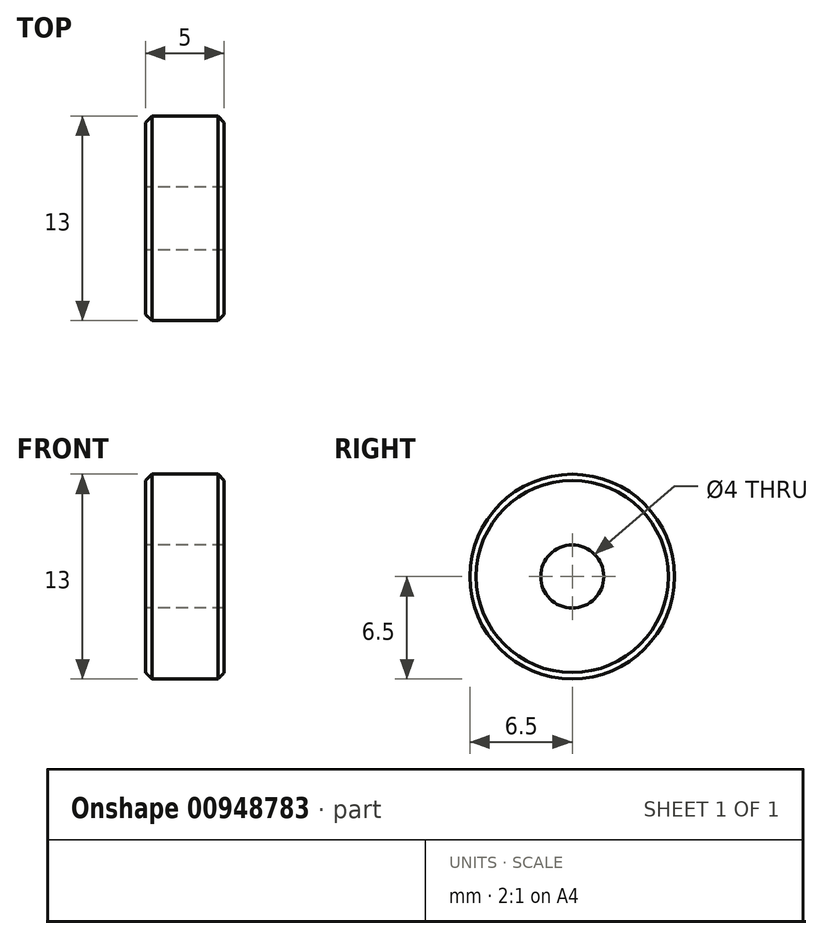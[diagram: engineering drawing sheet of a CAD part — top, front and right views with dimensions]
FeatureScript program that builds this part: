
annotation { "Feature Type Name" : "Feature", "Feature Type Description" : "" }
export const myFeature = defineFeature(function(context is Context, id is Id, definition is map)
    precondition{}
    {
        {
            var Q0;
            Q0=qCreatedBy(makeId("Right.planeOp"),FACE);
            var sketch = newSketch(context, id + "F0", { "sketchPlane" : qUnion([Q0])});
            skCircle(sketch, "E0", {"center": v(0, 0) * mm, "radius": 2 * mm});
            skCircle(sketch, "E1", {"center": v(0, 0) * mm, "radius": 6.5 * mm});
            skSolve(sketch);
        }
        {
            var Q0;
            Q0=makeQuery(id+"F0.imprint","IMPRINT",FACE,{"disambiguationData":[TD([[makeQuery(id+"F0.imprint","IMPRINT",EDGE,{"derivedFrom":sQuery(id+"F0.wireOp",EDGE,"E0")}),-1.0]])]});
            extrude(context, id + "F1", {"entities" : qUnion([Q0]), "depth" : 5 * mm, "offsetDistance" : 25 * mm});
        }
        {
            var Q0;
            Q0=makeQuery(id+"F1.opExtrude","SWEPT_FACE",FACE,{"disambiguationData":[OSD([sQuery(id+"F0.wireOp",EDGE,"E1")])]});
            chamfer(context, id + "F2", {"entities" : qUnion([Q0]), "width" : 0.4 * mm, "tangentPropagation" : true});
        }
    });
